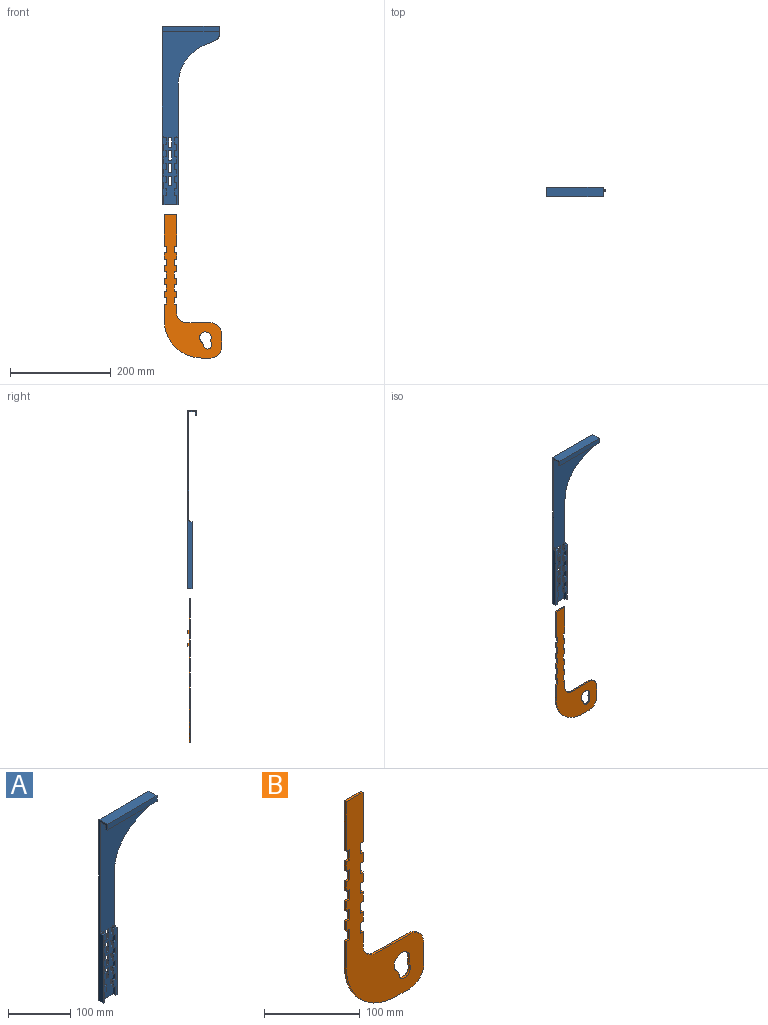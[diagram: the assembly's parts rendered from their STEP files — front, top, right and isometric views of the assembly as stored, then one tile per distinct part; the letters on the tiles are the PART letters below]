
ASSEMBLY  parts=2 mates=1
PART A: 106 faces, bbox 113x18.8x355.6 mm
  f0: plane 136.53x9.53mm, normal (1,0,0), area 848.9mm2, adj f4,f5,f6,f7,f10,f17,f18,f19
  f1: plane 133.35x7.62mm, normal (0,-1,0), area 705.6mm2, adj f6,f8,f11,f12,f13,f14,f15,f16
  f2: plane 12.7x4.45mm, normal (0,1,0), area 56.5mm2, adj f35,f39,f57,f61
  f3: plane 113.03x12.45mm, normal (0,0,-1), area 1406.8mm2, adj f4,f23,f25,f96
  f4: plane 352.43x113.03mm, normal (0,-1,0), area 13027.1mm2, adj f0,f3,f6,f23,f24,f25,f39,f44
  f5: plane 133.35x7.62mm, normal (0,-1,0), area 705.6mm2, adj f0,f6,f9,f17,f18,f19,f20,f21
  f6: plane 31.75x9.53mm, normal (0,0,-1), area 141.1mm2, adj f0,f1,f4,f5,f7,f23,f24,f39
  f7: plane 355.6x113.03mm, normal (0,1,0), area 14252.9mm2, adj f0,f6,f23,f24,f25,f26,f39,f44
  f8: plane 12.7x3.18mm, normal (-1,0,0), area 40.3mm2, adj f1,f11,f43,f60
  f9: plane 12.7x3.18mm, normal (1,0,0), area 40.3mm2, adj f5,f10,f17,f59
  f10: plane 12.7x4.45mm, normal (0,1,0), area 56.5mm2, adj f0,f9,f17,f59
  f11: plane 4.45x3.18mm, normal (0,0,-1), area 14.1mm2, adj f1,f8,f39,f43
  f12: plane 4.45x3.18mm, normal (0,0,1), area 14.1mm2, adj f1,f36,f39,f42
  f13: plane 4.45x3.18mm, normal (0,0,-1), area 14.1mm2, adj f1,f36,f39,f42
  f14: plane 4.45x3.18mm, normal (0,0,1), area 14.1mm2, adj f1,f37,f39,f41
  f15: plane 4.45x3.18mm, normal (0,0,-1), area 14.1mm2, adj f1,f37,f39,f41
  f16: plane 4.45x3.18mm, normal (0,0,1), area 14.1mm2, adj f1,f38,f39,f40
  f17: plane 4.45x3.18mm, normal (0,0,-1), area 14.1mm2, adj f0,f5,f9,f10
  f18: plane 4.45x3.18mm, normal (0,0,1), area 14.1mm2, adj f0,f5,f28,f33
  f19: plane 4.45x3.18mm, normal (0,0,-1), area 14.1mm2, adj f0,f5,f28,f33
  f20: plane 4.45x3.18mm, normal (0,0,1), area 14.1mm2, adj f0,f5,f29,f31
  f21: plane 4.45x3.18mm, normal (0,0,1), area 14.1mm2, adj f0,f5,f30,f32
  f22: plane 4.45x3.18mm, normal (0,0,-1), area 14.1mm2, adj f0,f5,f30,f32
  f23: plane 355.6x18.8mm, normal (-1,0,0), area 2051.8mm2, adj f3,f4,f5,f6,f7,f26,f56,f95
  f24: plane 239.67x9.53mm, normal (1,0,0), area 1609.9mm2, adj f1,f4,f6,f7,f57,f98,f101
  f25: plane 18.8x16.94mm, normal (1,0,0), area 127.6mm2, adj f3,f4,f7,f26,f95,f96,f97,f99
  f26: plane 113.03x18.8mm, normal (0,0,1), area 2124.5mm2, adj f7,f23,f25,f95
  f27: plane 12.7x3.18mm, normal (1,0,0), area 40.3mm2, adj f5,f34,f56,f58
  f28: plane 12.7x3.18mm, normal (1,0,0), area 40.3mm2, adj f5,f18,f19,f33
  f29: plane 12.7x3.18mm, normal (1,0,0), area 40.3mm2, adj f5,f20,f31,f103
  f30: plane 12.7x3.18mm, normal (1,0,0), area 40.3mm2, adj f5,f21,f22,f32
  f31: plane 12.7x4.45mm, normal (0,1,0), area 56.5mm2, adj f0,f20,f29,f103
  f32: plane 12.7x4.45mm, normal (0,1,0), area 56.5mm2, adj f0,f21,f22,f30
  f33: plane 12.7x4.45mm, normal (0,1,0), area 56.5mm2, adj f0,f18,f19,f28
  f34: plane 12.7x4.45mm, normal (0,1,0), area 56.5mm2, adj f0,f27,f56,f58
  f35: plane 12.7x3.18mm, normal (-1,0,0), area 40.3mm2, adj f1,f2,f57,f61
  f36: plane 12.7x3.18mm, normal (-1,0,0), area 40.3mm2, adj f1,f12,f13,f42
  f37: plane 12.7x3.18mm, normal (-1,0,0), area 40.3mm2, adj f1,f14,f15,f41
  f38: plane 12.7x3.18mm, normal (-1,0,0), area 40.3mm2, adj f1,f16,f40,f102
  f39: plane 136.53x9.53mm, normal (-1,0,0), area 848.9mm2, adj f1,f2,f4,f6,f7,f11,f12,f13
  f40: plane 12.7x4.45mm, normal (0,1,0), area 56.5mm2, adj f16,f38,f39,f102
  f41: plane 12.7x4.45mm, normal (0,1,0), area 56.5mm2, adj f14,f15,f37,f39
  f42: plane 12.7x4.45mm, normal (0,1,0), area 56.5mm2, adj f12,f13,f36,f39
  f43: plane 12.7x4.45mm, normal (0,1,0), area 56.5mm2, adj f8,f11,f39,f60
  f44: plane 19.05x3.18mm, normal (1,0,0), area 60.5mm2, adj f4,f7,f45,f47
  f45: plane 6.35x3.18mm, normal (0,0,1), area 20.2mm2, adj f4,f7,f44,f46
  f46: plane 19.05x3.18mm, normal (-1,0,0), area 60.5mm2, adj f4,f7,f45,f47
  f47: plane 6.35x3.18mm, normal (0,0,-1), area 20.2mm2, adj f4,f7,f44,f46
  f48: plane 19.05x3.18mm, normal (1,0,0), area 60.5mm2, adj f4,f7,f49,f51
  f49: plane 6.35x3.18mm, normal (0,0,1), area 20.2mm2, adj f4,f7,f48,f50
  f50: plane 19.05x3.18mm, normal (-1,0,0), area 60.5mm2, adj f4,f7,f49,f51
  f51: plane 6.35x3.18mm, normal (0,0,-1), area 20.2mm2, adj f4,f7,f48,f50
  f52: plane 19.05x3.18mm, normal (1,0,0), area 60.5mm2, adj f4,f7,f53,f55
  f53: plane 6.35x3.18mm, normal (0,0,1), area 20.2mm2, adj f4,f7,f52,f54
  f54: plane 19.05x3.18mm, normal (-1,0,0), area 60.5mm2, adj f4,f7,f53,f55
  f55: plane 6.35x3.18mm, normal (0,0,-1), area 20.2mm2, adj f4,f7,f52,f54
  f56: plane 7.62x3.18mm, normal (0,0,1), area 24.2mm2, adj f5,f23,f27,f34,f100
  f57: plane 7.62x3.18mm, normal (0,0,1), area 24.2mm2, adj f1,f2,f24,f35,f101
  f58: plane 4.45x3.18mm, normal (0,0,-1), area 14.1mm2, adj f0,f5,f27,f34
  f59: plane 4.45x3.18mm, normal (0,0,1), area 14.1mm2, adj f0,f5,f9,f10
  f60: plane 4.45x3.18mm, normal (0,0,1), area 14.1mm2, adj f1,f8,f39,f43
  f61: plane 4.45x3.18mm, normal (0,0,-1), area 14.1mm2, adj f1,f2,f35,f39
  f62: plane 19.05x3.18mm, normal (1,0,0), area 60.5mm2, adj f4,f7,f63,f65
  f63: plane 6.35x3.18mm, normal (0,0,1), area 20.2mm2, adj f4,f7,f62,f64
  f64: plane 19.05x3.18mm, normal (-1,0,0), area 60.5mm2, adj f4,f7,f63,f65
  f65: plane 6.35x3.18mm, normal (0,0,-1), area 20.2mm2, adj f4,f7,f62,f64
  f66: plane 4.45x3.18mm, normal (0,0,1), area 14.1mm2, adj f4,f7,f39,f67
  f67: plane 12.7x3.18mm, normal (1,0,0), area 40.3mm2, adj f4,f7,f66,f68
  f68: plane 4.45x3.18mm, normal (0,0,-1), area 14.1mm2, adj f4,f7,f39,f67
  f69: plane 4.45x3.18mm, normal (0,0,1), area 14.1mm2, adj f4,f7,f39,f70
  f70: plane 12.7x3.18mm, normal (1,0,0), area 40.3mm2, adj f4,f7,f69,f71
  f71: plane 4.45x3.18mm, normal (0,0,-1), area 14.1mm2, adj f4,f7,f39,f70
  f72: plane 4.45x3.18mm, normal (0,0,1), area 14.1mm2, adj f0,f4,f7,f74
  f73: plane 4.45x3.18mm, normal (0,0,-1), area 14.1mm2, adj f0,f4,f7,f74
  f74: plane 12.7x3.18mm, normal (-1,0,0), area 40.3mm2, adj f4,f7,f72,f73
  f75: plane 4.45x3.18mm, normal (0,0,1), area 14.1mm2, adj f0,f4,f7,f77
  f76: plane 4.45x3.18mm, normal (0,0,-1), area 14.1mm2, adj f0,f4,f7,f77
  f77: plane 12.7x3.18mm, normal (-1,0,0), area 40.3mm2, adj f4,f7,f75,f76
  f78: plane 4.45x3.18mm, normal (0,0,1), area 14.1mm2, adj f0,f4,f7,f80
  f79: plane 4.45x3.18mm, normal (0,0,-1), area 14.1mm2, adj f0,f4,f7,f80
  f80: plane 12.7x3.18mm, normal (-1,0,0), area 40.3mm2, adj f4,f7,f78,f79
  f81: plane 4.45x3.18mm, normal (0,0,1), area 14.1mm2, adj f4,f7,f39,f82
  f82: plane 12.7x3.18mm, normal (1,0,0), area 40.3mm2, adj f4,f7,f81,f83
  f83: plane 4.45x3.18mm, normal (0,0,-1), area 14.1mm2, adj f4,f7,f39,f82
  f84: plane 4.45x3.18mm, normal (0,0,1), area 14.1mm2, adj f0,f4,f7,f86
  f85: plane 4.45x3.18mm, normal (0,0,-1), area 14.1mm2, adj f0,f4,f7,f86
  f86: plane 12.7x3.18mm, normal (-1,0,0), area 40.3mm2, adj f4,f7,f84,f85
  f87: plane 4.45x3.18mm, normal (0,0,1), area 14.1mm2, adj f4,f7,f39,f88
  f88: plane 12.7x3.18mm, normal (1,0,0), area 40.3mm2, adj f4,f7,f87,f89
  f89: plane 4.45x3.18mm, normal (0,0,-1), area 14.1mm2, adj f4,f7,f39,f88
  f90: plane 4.45x3.18mm, normal (0,0,-1), area 14.1mm2, adj f0,f4,f7,f91
  f91: plane 12.7x3.18mm, normal (-1,0,0), area 40.3mm2, adj f4,f7,f90,f105
  f92: plane 12.7x3.18mm, normal (1,0,0), area 40.3mm2, adj f4,f7,f93,f104
  f93: plane 4.45x3.18mm, normal (0,0,-1), area 14.1mm2, adj f4,f7,f39,f92
  f94: plane 22.17x9.47mm, normal (0.39,0,-0.92), area 76.6mm2, adj f4,f7,f98,f99
  f95: plane 113.03x10.8mm, normal (0,-1,0), area 1220.2mm2, adj f23,f25,f26,f97
  f96: plane 113.03x7.62mm, normal (0,1,0), area 861.3mm2, adj f3,f23,f25,f97
  f97: plane 113.03x3.18mm, normal (0,0,-1), area 358.9mm2, adj f23,f25,f95,f96
  f98: cylinder r=84.53mm len=77.74mm, axis (0,-1,0), area 313.2mm2, adj f4,f7,f24,f94
  f99: cylinder r=12.81mm len=11.78mm, axis (0,1,0), area 47.5mm2, adj f4,f7,f25,f94
  f100: cylinder r=3.17mm len=3.18mm, axis (-1,0,0), area 15.8mm2, adj f0,f4,f23,f56
  f101: cylinder r=3.17mm len=3.18mm, axis (-1,0,0), area 15.8mm2, adj f4,f24,f39,f57
  f102: plane 4.45x3.18mm, normal (0,0,-1), area 14.1mm2, adj f1,f38,f39,f40
  f103: plane 4.45x3.18mm, normal (0,0,-1), area 14.1mm2, adj f0,f5,f29,f31
  f104: plane 4.45x3.18mm, normal (0,0,1), area 14.1mm2, adj f4,f7,f39,f92
  f105: plane 4.45x3.18mm, normal (0,0,1), area 14.1mm2, adj f0,f4,f7,f91
PART B: 70 faces, bbox 114.3x6.4x285.5 mm
  f0: plane 4.45x2.79mm, normal (0,0,1), area 12.4mm2, adj f4,f5,f57,f63
  f1: plane 4.45x2.79mm, normal (0,0,-1), area 12.4mm2, adj f4,f5,f57,f62
  f2: plane 12.19x2.79mm, normal (-1,0,0), area 34.1mm2, adj f4,f5,f50,f54
  f3: plane 12.19x2.79mm, normal (-1,0,0), area 34.1mm2, adj f4,f5,f22,f51
  f4: plane 285.5x114.3mm, normal (0,-1,0), area 10858.6mm2, adj f0,f1,f2,f3,f6,f7,f8,f9
  f5: plane 285.5x114.3mm, normal (0,1,0), area 10784.3mm2, adj f0,f1,f2,f3,f6,f7,f8,f9
  f6: plane 32.51x2.79mm, normal (-1,0,0), area 90.8mm2, adj f4,f5,f46,f53
  f7: plane 26.92x2.79mm, normal (1,0,0), area 75.2mm2, adj f4,f5,f44,f45
  f8: plane 63.37x2.79mm, normal (-1,0,0), area 177mm2, adj f4,f5,f32,f69
  f9: plane 12.19x2.79mm, normal (-1,0,0), area 34.1mm2, adj f4,f5,f30,f31
  f10: plane 12.19x2.79mm, normal (-1,0,0), area 34.1mm2, adj f4,f5,f23,f29
  f11: plane 6.1x3.56mm, normal (-1,0,0), area 21.7mm2, adj f5,f12,f14,f15
  f12: plane 6.1x3.56mm, normal (0,0,1), area 21.7mm2, adj f5,f11,f13,f15
  f13: plane 6.1x3.56mm, normal (1,0,0), area 21.7mm2, adj f5,f12,f14,f15
  f14: plane 6.1x3.56mm, normal (0,0,-1), area 21.7mm2, adj f5,f11,f13,f15
  f15: plane 6.1x6.1mm, normal (0,1,0), area 37.2mm2, adj f11,f12,f13,f14
  f16: plane 6.1x3.56mm, normal (1,0,0), area 21.7mm2, adj f5,f18,f19,f20
  f17: plane 6.1x3.56mm, normal (-1,0,0), area 21.7mm2, adj f5,f18,f19,f20
  f18: plane 6.1x6.1mm, normal (0,1,0), area 37.2mm2, adj f16,f17,f19,f20
  f19: plane 6.1x3.56mm, normal (0,0,-1), area 21.7mm2, adj f5,f16,f17,f18
  f20: plane 6.1x3.56mm, normal (0,0,1), area 21.7mm2, adj f5,f16,f17,f18
  f21: plane 13.21x2.79mm, normal (-1,0,0), area 36.9mm2, adj f4,f5,f22,f23
  f22: plane 4.45x2.79mm, normal (0,0,1), area 12.4mm2, adj f3,f4,f5,f21
  f23: plane 4.45x2.79mm, normal (0,0,-1), area 12.4mm2, adj f4,f5,f10,f21
  f24: plane 4.45x2.79mm, normal (0,0,1), area 12.4mm2, adj f4,f5,f59,f65
  f25: plane 4.45x2.79mm, normal (0,0,-1), area 12.4mm2, adj f4,f5,f59,f64
  f26: plane 4.45x2.79mm, normal (0,0,1), area 12.4mm2, adj f4,f5,f58,f64
  f27: plane 4.45x2.79mm, normal (0,0,-1), area 12.4mm2, adj f4,f5,f58,f63
  f28: plane 13.21x2.79mm, normal (-1,0,0), area 36.9mm2, adj f4,f5,f29,f30
  f29: plane 4.45x2.79mm, normal (0,0,1), area 12.4mm2, adj f4,f5,f10,f28
  f30: plane 4.45x2.79mm, normal (0,0,-1), area 12.4mm2, adj f4,f5,f9,f28
  f31: plane 4.45x2.79mm, normal (0,0,1), area 12.4mm2, adj f4,f5,f9,f33
  f32: plane 4.45x2.79mm, normal (0,0,-1), area 12.4mm2, adj f4,f5,f8,f33
  f33: plane 13.21x2.79mm, normal (-1,0,0), area 36.9mm2, adj f4,f5,f31,f32
  f34: plane 47.63x2.79mm, normal (0,0,1), area 133.1mm2, adj f4,f5,f44,f68
  f35: plane 18.03x2.79mm, normal (0,0,-1), area 50.4mm2, adj f4,f5,f45,f46
  f36: plane 2.79x2.49mm, normal (-0.97,0,-0.23), area 7.1mm2, adj f4,f5,f40,f43
  f37: cylinder r=11.43mm len=22.86mm, axis (0,-1,0), area 140.4mm2, adj f4,f5,f42,f43
  f38: plane 2.79x2.42mm, normal (0.95,0,0.32), area 7.1mm2, adj f4,f5,f41,f42
  f39: cylinder r=8.38mm len=16.72mm, axis (0,-1,0), area 81.7mm2, adj f4,f5,f40,f41
  f40: cylinder r=6.35mm len=2.79mm, axis (0,-1,0), area 4mm2, adj f4,f5,f36,f39
  f41: cylinder r=6.35mm len=2.79mm, axis (0,-1,0), area 4mm2, adj f4,f5,f38,f39
  f42: cylinder r=5.08mm len=2.79mm, axis (0,-1,0), area 8.2mm2, adj f4,f5,f37,f38
  f43: cylinder r=5.08mm len=2.88mm, axis (0,-1,0), area 8.2mm2, adj f4,f5,f36,f37
  f44: cylinder r=21.46mm len=21.46mm, axis (0,-1,0), area 94.2mm2, adj f4,f5,f7,f34
  f45: cylinder r=21.46mm len=21.46mm, axis (0,1,0), area 94.2mm2, adj f4,f5,f7,f35
  f46: cylinder r=74.81mm len=74.81mm, axis (0,1,0), area 328.3mm2, adj f4,f5,f6,f35
  f47: plane 4.45x2.79mm, normal (0,0,1), area 12.4mm2, adj f4,f5,f60,f66
  f48: plane 4.45x2.79mm, normal (0,0,-1), area 12.4mm2, adj f4,f5,f60,f65
  f49: plane 13.21x2.79mm, normal (-1,0,0), area 36.9mm2, adj f4,f5,f50,f51
  f50: plane 4.45x2.79mm, normal (0,0,1), area 12.4mm2, adj f2,f4,f5,f49
  f51: plane 4.45x2.79mm, normal (0,0,-1), area 12.4mm2, adj f3,f4,f5,f49
  f52: plane 13.21x2.79mm, normal (-1,0,0), area 36.9mm2, adj f4,f5,f53,f54
  f53: plane 4.45x2.79mm, normal (0,0,1), area 12.4mm2, adj f4,f5,f6,f52
  f54: plane 4.45x2.79mm, normal (0,0,-1), area 12.4mm2, adj f2,f4,f5,f52
  f55: plane 4.45x2.79mm, normal (0,0,1), area 12.4mm2, adj f4,f5,f61,f67
  f56: plane 4.45x2.79mm, normal (0,0,-1), area 12.4mm2, adj f4,f5,f61,f66
  f57: plane 13.21x2.79mm, normal (1,0,0), area 36.9mm2, adj f0,f1,f4,f5
  f58: plane 13.21x2.79mm, normal (1,0,0), area 36.9mm2, adj f4,f5,f26,f27
  f59: plane 13.21x2.79mm, normal (1,0,0), area 36.9mm2, adj f4,f5,f24,f25
  f60: plane 13.21x2.79mm, normal (1,0,0), area 36.9mm2, adj f4,f5,f47,f48
  f61: plane 13.21x2.79mm, normal (1,0,0), area 36.9mm2, adj f4,f5,f55,f56
  f62: plane 63.37x2.79mm, normal (1,0,0), area 177mm2, adj f1,f4,f5,f69
  f63: plane 12.19x2.79mm, normal (1,0,0), area 34.1mm2, adj f0,f4,f5,f27
  f64: plane 12.19x2.79mm, normal (1,0,0), area 34.1mm2, adj f4,f5,f25,f26
  f65: plane 12.19x2.79mm, normal (1,0,0), area 34.1mm2, adj f4,f5,f24,f48
  f66: plane 12.19x2.79mm, normal (1,0,0), area 34.1mm2, adj f4,f5,f47,f56
  f67: plane 17.15x2.79mm, normal (1,0,0), area 47.9mm2, adj f4,f5,f55,f68
  f68: cylinder r=20.32mm len=20.32mm, axis (0,-1,0), area 89.2mm2, adj f4,f5,f34,f67
  f69: plane 24.89x2.79mm, normal (0,0,1), area 69.5mm2, adj f4,f5,f8,f62
PLACE A t=(-126.88,-132.39,26.05)mm
PLACE B t=(-271.48,-132.77,-272.62)mm
MATE planar B.f15 <-> A.f7  axis (0,1,0) through (-107.83,-132.39,-412.35)mm
